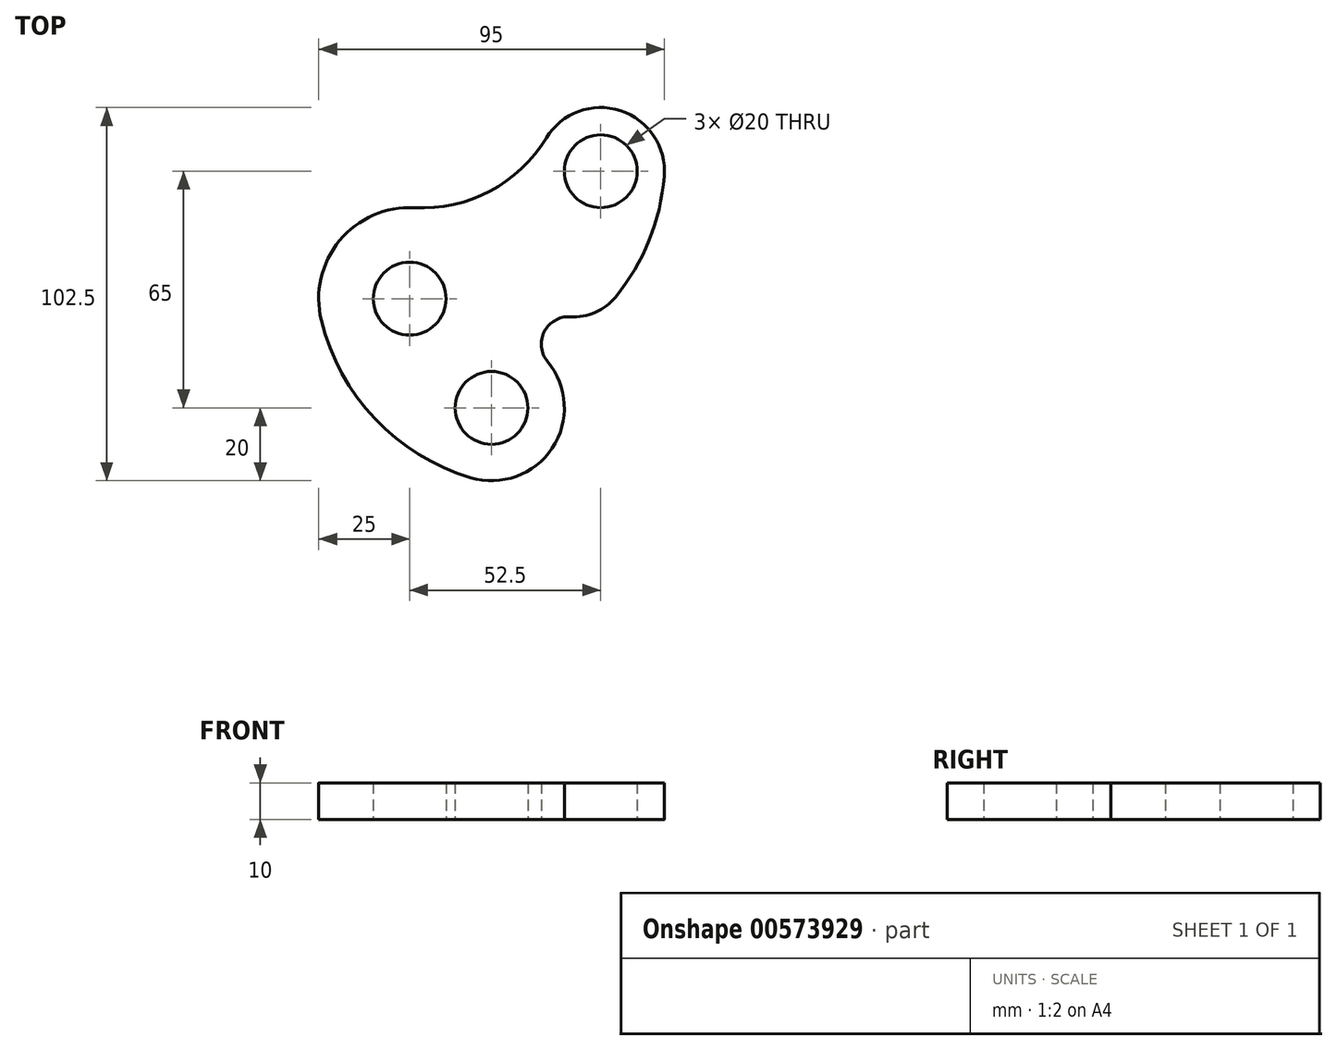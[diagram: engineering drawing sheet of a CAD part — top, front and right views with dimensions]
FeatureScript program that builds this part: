
annotation { "Feature Type Name" : "Feature", "Feature Type Description" : "" }
export const myFeature = defineFeature(function(context is Context, id is Id, definition is map)
    precondition{}
    {
        {
            var Q0;
            Q0=qCreatedBy(makeId("Top.planeOp"),FACE);
            var sketch = newSketch(context, id + "F0", { "sketchPlane" : qUnion([Q0])});
            skCircle(sketch, "E0", {"center": v(0, 0) * mm, "radius": 10 * mm});
            skCircle(sketch, "E1", {"center": v(22.5, -30) * mm, "radius": 10 * mm});
            skCircle(sketch, "E2", {"center": v(52.5, 35) * mm, "radius": 10 * mm});
            skArc(sketch, "E3", {"start": v(1.3, 24.97) * mm, "mid": v(-19.26, 15.94) * mm, "end": v(-24.28, -5.94) * mm});
            skArc(sketch, "E4", {"start": v(16.75, -49.16) * mm, "mid": v(39.17, -41.05) * mm, "end": v(37.9, -17.24) * mm});
            skArc(sketch, "E5", {"start": v(69.94, 33.58) * mm, "mid": v(57.9, 51.64) * mm, "end": v(37.55, 44.1) * mm});
            skArc(sketch, "E6", {"start": v(1.3, 24.97) * mm, "mid": v(22.07, 29.54) * mm, "end": v(37.55, 44.1) * mm});
            skArc(sketch, "E7", {"start": v(-24.28, -5.94) * mm, "mid": v(-9.51, -33) * mm, "end": v(16.75, -49.16) * mm});
            skArc(sketch, "E8", {"start": v(44.12, -4.97) * mm, "mid": v(51.03, -3.73) * mm, "end": v(56.62, 0.51) * mm});
            skArc(sketch, "E9", {"start": v(44.12, -4.97) * mm, "mid": v(37, -9.07) * mm, "end": v(37.9, -17.24) * mm});
            skArc(sketch, "E10", {"start": v(56.62, 0.51) * mm, "mid": v(65.8, 16.03) * mm, "end": v(69.94, 33.58) * mm});
            skSolve(sketch);
        }
        {
            var Q0;
            Q0=makeQuery(id+"F0.imprint","IMPRINT",FACE,{"disambiguationData":[TD([[makeQuery(id+"F0.imprint","IMPRINT",EDGE,{"derivedFrom":sQuery(id+"F0.wireOp",EDGE,"E0")}),-1.0]])]});
            extrude(context, id + "F1", {"entities" : qUnion([Q0]), "depth" : 10 * mm, "offsetDistance" : 25 * mm});
        }
    });
